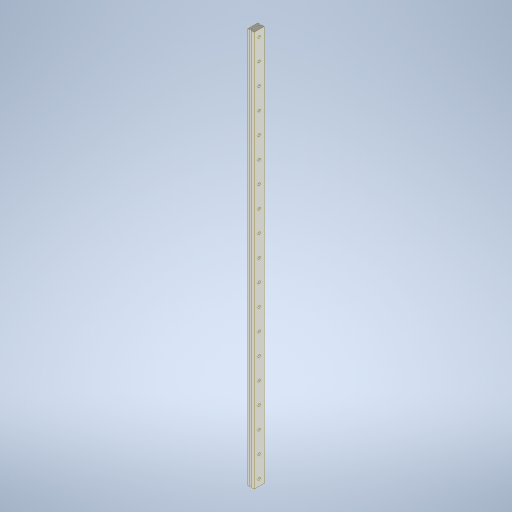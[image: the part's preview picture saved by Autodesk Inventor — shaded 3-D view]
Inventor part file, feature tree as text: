
AUTODESK INVENTOR PART (.ipt)
format: ipt  version: 2023 (Build 270158000, 158)  size: 310,272 bytes
history: native  units: mm
features: sketch x2, other x1, extrude x1, hole x1
ambient origin geometry x8: Origin, YZ Plane, XZ Plane, XY Plane, X Axis, Y Axis, Z Axis, Center Point
bodies: Body1 (feature_tree)
feature tree (5):
  other  "Sólido1"
  extrude  "Extrusão1"  Depth=469.0mm TaperAngle=0.0deg
  hole  "Furo1"  [1 undecoded]
  sketch  "Esboço1"  dims[d0=7.5mm d1=12.0mm d2=8.0mm d3=1.0mm d4=3.5mm d5=0.5mm d6=469.0mm d7=0.0mm]
  sketch  "Esboço2"  dims[d8=190.0mm d10=25.2mm d11=10.0mm d13=10.0mm d18=6.0mm d19=3.0mm d20=13.0mm d21=4.0mm d22=2.0mm d23=90.0deg d24=0.5mm d25=20.594885mm d27=453.6mm d28=469.0mm d29=7.7mm]
note: 1 required parameter value undecoded (feature->parameter linkage not recoverable at this tier; creation-order binding heuristic only, values carry confidence <= 0.55)
